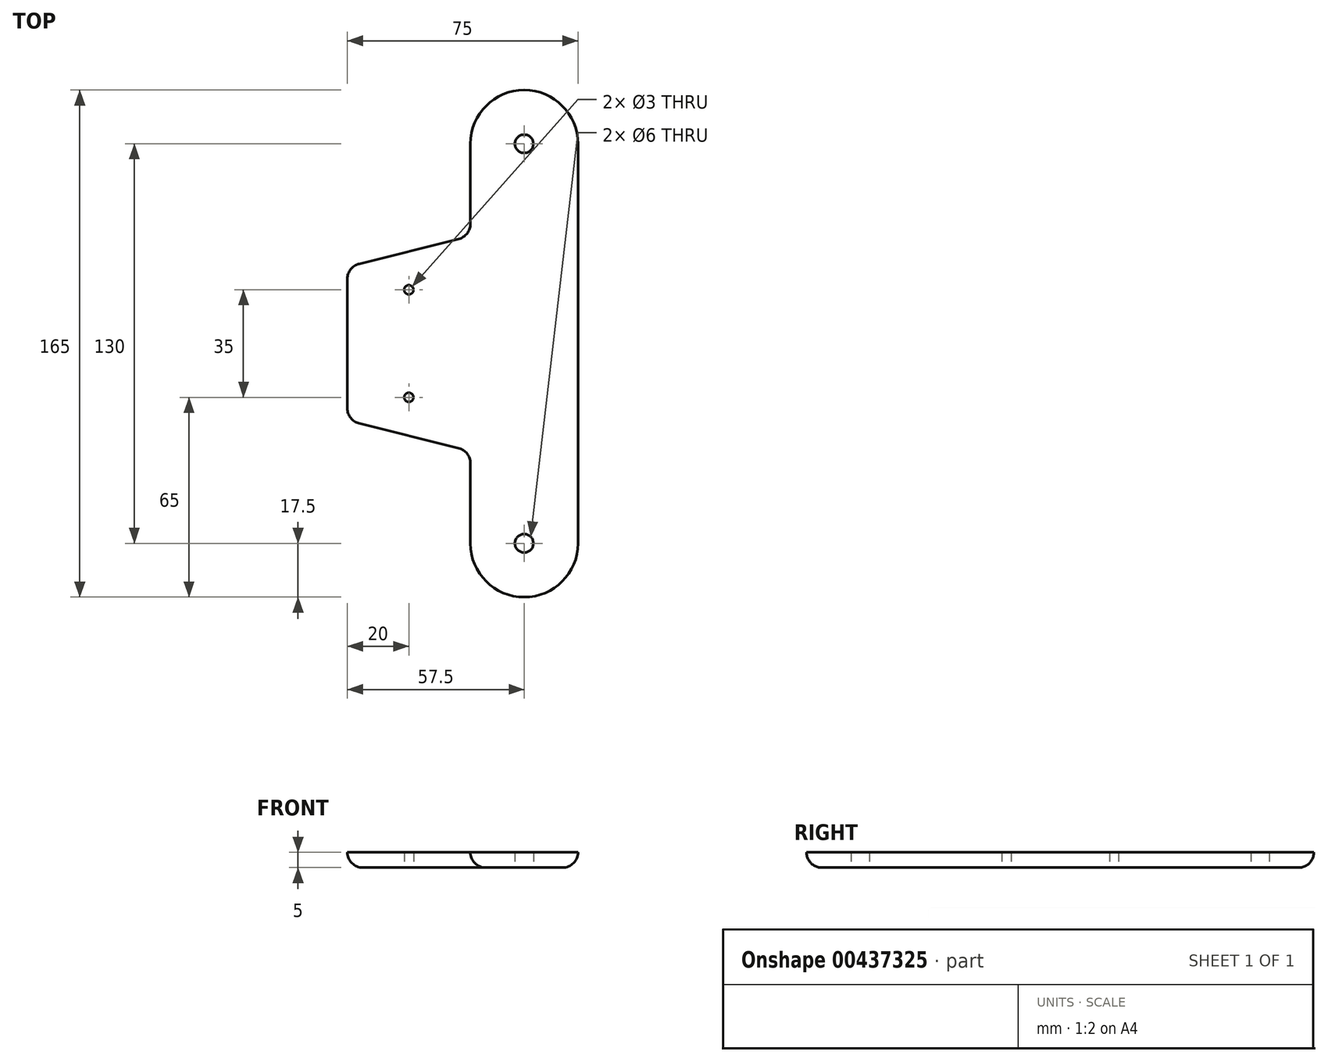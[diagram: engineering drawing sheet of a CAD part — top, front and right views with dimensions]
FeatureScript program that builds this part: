
annotation { "Feature Type Name" : "Feature", "Feature Type Description" : "" }
export const myFeature = defineFeature(function(context is Context, id is Id, definition is map)
    precondition{}
    {
        {
            var Q0;
            Q0=qCreatedBy(makeId("Top.planeOp"),FACE);
            var sketch = newSketch(context, id + "F0", { "sketchPlane" : qUnion([Q0])});
            skLineSegment(sketch, "E0.left", {"start": v(17.5, 65) * mm, "end": v(17.5, -65) * mm});
            skLineSegment(sketch, "E0.right", {"start": v(-17.5, 65) * mm, "end": v(-17.5, 38.9) * mm});
            skPoint(sketch, "E0.middle", {"position": v(0, 0) * mm});
            skArc(sketch, "E1", {"start": v(-17.5, -65) * mm, "mid": v(0, -82.5) * mm, "end": v(17.5, -65) * mm});
            skLineSegment(sketch, "E2.0", {"start": v(-57.5, 21.1) * mm, "end": v(-57.5, -21.1) * mm});
            skArc(sketch, "E3", {"start": v(17.5, 65) * mm, "mid": v(0, 82.5) * mm, "end": v(-17.5, 65) * mm});
            skLineSegment(sketch, "E4", {"start": v(-53.71, -25.95) * mm, "end": v(-21.29, -34.05) * mm});
            skLineSegment(sketch, "E5", {"start": v(-53.71, 25.95) * mm, "end": v(-21.29, 34.05) * mm});
            skLineSegment(sketch, "E6.trimOffspring", {"start": v(-17.5, -38.9) * mm, "end": v(-17.5, -65) * mm});
            skPoint(sketch, "E7.visualSharp", {"position": v(-57.5, 25) * mm});
            skArc(sketch, "E7.filletArc", {"start": v(-53.71, 25.95) * mm, "mid": v(-56.44, 24.17) * mm, "end": v(-57.5, 21.1) * mm});
            skPoint(sketch, "E8.visualSharp", {"position": v(-57.5, -25) * mm});
            skArc(sketch, "E8.filletArc", {"start": v(-57.5, -21.1) * mm, "mid": v(-56.44, -24.17) * mm, "end": v(-53.71, -25.95) * mm});
            skPoint(sketch, "E9.visualSharp", {"position": v(-17.5, -35) * mm});
            skArc(sketch, "E9.filletArc", {"start": v(-17.5, -38.9) * mm, "mid": v(-18.56, -35.83) * mm, "end": v(-21.29, -34.05) * mm});
            skPoint(sketch, "E10.visualSharp", {"position": v(-17.5, 35) * mm});
            skArc(sketch, "E10.filletArc", {"start": v(-21.29, 34.05) * mm, "mid": v(-18.56, 35.83) * mm, "end": v(-17.5, 38.9) * mm});
            skPoint(sketch, "E11", {"position": v(-57.5, 0) * mm});
            skPoint(sketch, "E12", {"position": v(-37.5, 0) * mm});
            skCircle(sketch, "E13", {"center": v(-37.5, 17.5) * mm, "radius": 1.5 * mm});
            skLineSegment(sketch, "E14", {"start": v(-57.5, 0) * mm, "end": v(0, 0) * mm, "construction": true});
            skCircle(sketch, "E15.MirrorC", {"center": v(-37.5, -17.5) * mm, "radius": 1.5 * mm});
            skCircle(sketch, "E16", {"center": v(0, 65) * mm, "radius": 3 * mm});
            skCircle(sketch, "E17", {"center": v(0, -65) * mm, "radius": 3 * mm});
            skSolve(sketch);
        }
        {
            var Q0;
            Q0=makeQuery(id+"F0.imprint","IMPRINT",FACE,{"disambiguationData":[TD([[makeQuery(id+"F0.imprint","IMPRINT",EDGE,{"derivedFrom":sQuery(id+"F0.wireOp",EDGE,"E0.left")}),-1.0]])]});
            extrude(context, id + "F1", {"entities" : qUnion([Q0]), "depth" : 5 * mm});
        }
        {
            var Q0;
            Q0=makeQuery(id+"F1.opExtrude","CAP_EDGE",EDGE,{"disambiguationData":[OSD([sQuery(id+"F0.wireOp",EDGE,"E0.left")])],"isStart":true});
            fillet(context, id + "F2", {"entities" : qUnion([Q0]), "radius" : 5 * mm, "tangentPropagation" : true, "allowEdgeOverflow" : false});
        }
    });
